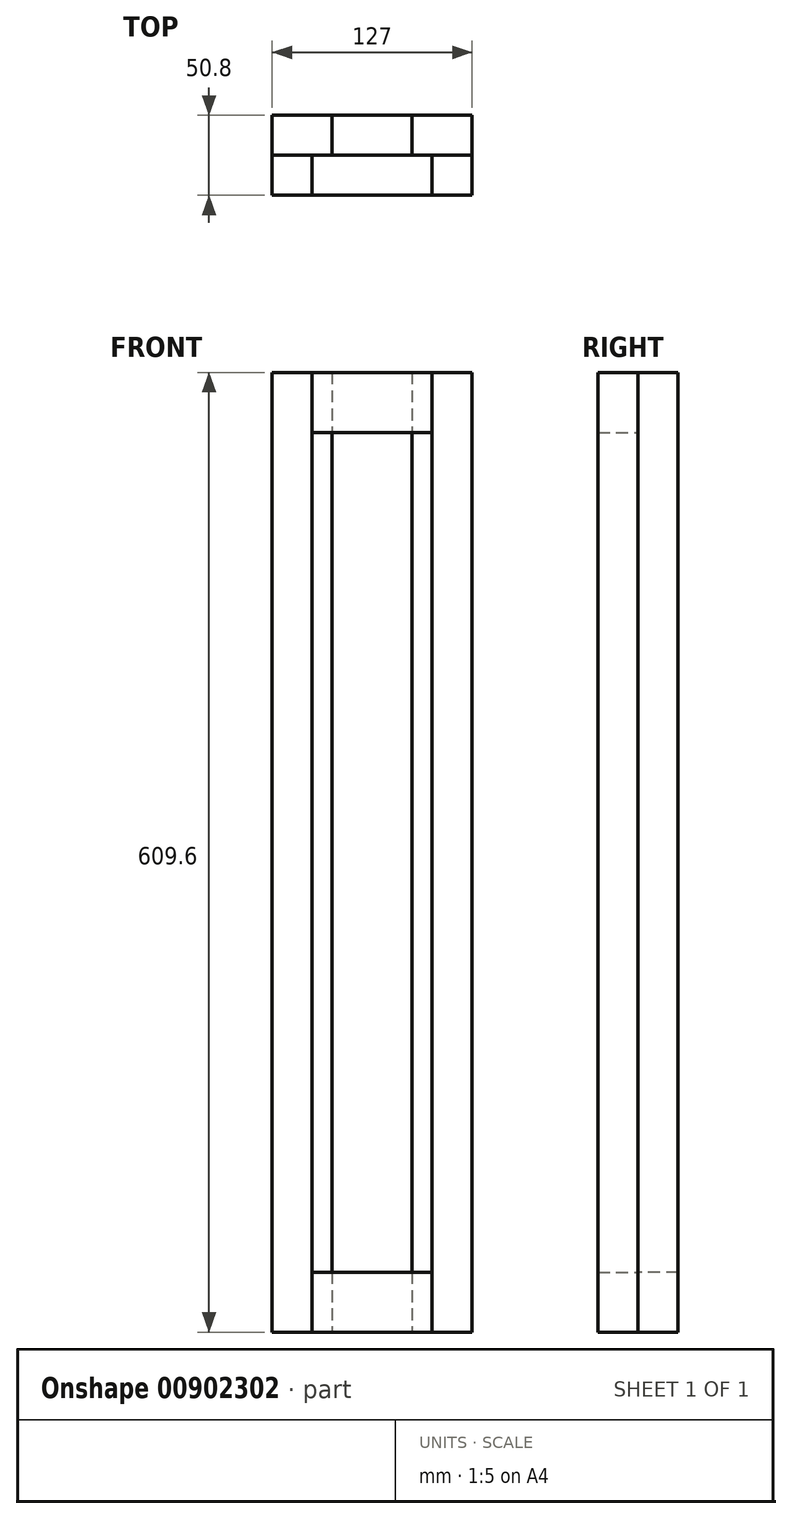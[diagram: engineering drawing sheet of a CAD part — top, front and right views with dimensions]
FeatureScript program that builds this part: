
annotation { "Feature Type Name" : "Feature", "Feature Type Description" : "" }
export const myFeature = defineFeature(function(context is Context, id is Id, definition is map)
    precondition{}
    {
        {
            var Q0;
            Q0=qCreatedBy(makeId("Front.planeOp"),FACE);
            var sketch = newSketch(context, id + "F0", { "sketchPlane" : qUnion([Q0])});
            skLineSegment(sketch, "E0.bottom", {"start": v(-63.5, 256.82) * mm, "end": v(-25.4, 256.82) * mm});
            skLineSegment(sketch, "E0.top", {"start": v(-63.5, -352.78) * mm, "end": v(-25.4, -352.78) * mm});
            skLineSegment(sketch, "E0.left", {"start": v(-63.5, 256.82) * mm, "end": v(-63.5, -352.78) * mm});
            skLineSegment(sketch, "E0.right", {"start": v(-25.4, 256.82) * mm, "end": v(-25.4, -352.78) * mm});
            skLineSegment(sketch, "E1.bottom", {"start": v(25.4, 256.82) * mm, "end": v(63.5, 256.82) * mm});
            skLineSegment(sketch, "E1.top", {"start": v(25.4, -352.78) * mm, "end": v(63.5, -352.78) * mm});
            skLineSegment(sketch, "E1.left", {"start": v(25.4, 256.82) * mm, "end": v(25.4, -352.78) * mm});
            skLineSegment(sketch, "E1.right", {"start": v(63.5, 256.82) * mm, "end": v(63.5, -352.78) * mm});
            skSolve(sketch);
        }
        {
            var Q0;
            Q0=makeQuery(id+"F0.imprint","IMPRINT",FACE,{"disambiguationData":[TD([[makeQuery(id+"F0.imprint","IMPRINT",EDGE,{"derivedFrom":sQuery(id+"F0.wireOp",EDGE,"E1.bottom")}),-1.0]])]});
            var Q1;
            Q1=makeQuery(id+"F0.imprint","IMPRINT",FACE,{"disambiguationData":[TD([[makeQuery(id+"F0.imprint","IMPRINT",EDGE,{"derivedFrom":sQuery(id+"F0.wireOp",EDGE,"E0.bottom")}),-1.0]])]});
            extrude(context, id + "F1", {"entities" : qUnion([Q0, Q1]), "oppositeDirection" : true, "depth" : 25.4 * mm, "offsetDistance" : 25.4 * mm});
        }
        {
            var Q0;
            Q0=qCreatedBy(makeId("Front.planeOp"),FACE);
            var sketch = newSketch(context, id + "F2", { "sketchPlane" : qUnion([Q0])});
            skLineSegment(sketch, "E2.bottom", {"start": v(-63.5, 256.82) * mm, "end": v(-38.1, 256.82) * mm});
            skLineSegment(sketch, "E2.top", {"start": v(-63.5, -352.78) * mm, "end": v(-38.1, -352.78) * mm});
            skLineSegment(sketch, "E2.left", {"start": v(-63.5, 256.82) * mm, "end": v(-63.5, -352.78) * mm});
            skLineSegment(sketch, "E2.right", {"start": v(-38.1, 256.82) * mm, "end": v(-38.1, -352.78) * mm});
            skLineSegment(sketch, "E3.bottom", {"start": v(38.1, 256.82) * mm, "end": v(63.5, 256.82) * mm});
            skLineSegment(sketch, "E3.top", {"start": v(38.1, -352.78) * mm, "end": v(63.5, -352.78) * mm});
            skLineSegment(sketch, "E3.left", {"start": v(38.1, 256.82) * mm, "end": v(38.1, -352.78) * mm});
            skLineSegment(sketch, "E3.right", {"start": v(63.5, 256.82) * mm, "end": v(63.5, -352.78) * mm});
            skLineSegment(sketch, "E4.bottom", {"start": v(-38.1, 256.82) * mm, "end": v(38.1, 256.82) * mm});
            skLineSegment(sketch, "E4.top", {"start": v(-38.1, 218.72) * mm, "end": v(38.1, 218.72) * mm});
            skLineSegment(sketch, "E4.left", {"start": v(-38.1, 256.82) * mm, "end": v(-38.1, 218.72) * mm});
            skLineSegment(sketch, "E4.right", {"start": v(38.1, 256.82) * mm, "end": v(38.1, 218.72) * mm});
            skLineSegment(sketch, "E5.bottom", {"start": v(-38.1, -314.68) * mm, "end": v(38.1, -314.68) * mm});
            skLineSegment(sketch, "E5.top", {"start": v(-38.1, -352.78) * mm, "end": v(38.1, -352.78) * mm});
            skLineSegment(sketch, "E5.left", {"start": v(-38.1, -314.68) * mm, "end": v(-38.1, -352.78) * mm});
            skLineSegment(sketch, "E5.right", {"start": v(38.1, -314.68) * mm, "end": v(38.1, -352.78) * mm});
            skSolve(sketch);
        }
        {
            var Q0;
            Q0=makeQuery(id+"F2.imprint","IMPRINT",FACE,{"disambiguationData":[TD([[makeQuery(id+"F2.imprint","IMPRINT",EDGE,{"derivedFrom":sQuery(id+"F2.wireOp",EDGE,"E2.bottom")}),-1.0]])]});
            var Q1;
            Q1=makeQuery(id+"F2.imprint","IMPRINT",FACE,{"disambiguationData":[TD([[makeQuery(id+"F2.imprint","IMPRINT",EDGE,{"derivedFrom":sQuery(id+"F2.wireOp",EDGE,"E3.bottom")}),-1.0]])]});
            extrude(context, id + "F3", {"entities" : qUnion([Q0, Q1]), "depth" : 25.4 * mm, "offsetDistance" : 25.4 * mm});
        }
        {
            var Q0;
            Q0=makeQuery(id+"F2.imprint","IMPRINT",FACE,{"disambiguationData":[TD([[makeQuery(id+"F2.imprint","IMPRINT",EDGE,{"derivedFrom":sQuery(id+"F2.wireOp",EDGE,"E4.bottom")}),-1.0]])]});
            var Q1;
            Q1=makeQuery(id+"F2.imprint","IMPRINT",FACE,{"disambiguationData":[TD([[makeQuery(id+"F2.imprint","IMPRINT",EDGE,{"derivedFrom":sQuery(id+"F2.wireOp",EDGE,"E5.bottom")}),-1.0]])]});
            extrude(context, id + "F4", {"entities" : qUnion([Q0, Q1]), "depth" : 25.4 * mm, "offsetDistance" : 25.4 * mm});
        }
        {
            var Q0;
            Q0=makeQuery(id+"F4.opExtrude","CAP_FACE",FACE,{"disambiguationData":[OSD([sQuery(id+"F2.wireOp",EDGE,"E5.bottom"),sQuery(id+"F2.wireOp",EDGE,"E5.top"),sQuery(id+"F2.wireOp",EDGE,"E5.left"),sQuery(id+"F2.wireOp",EDGE,"E5.right")])],"isStart":true});
            var sketch = newSketch(context, id + "F5", { "sketchPlane" : qUnion([Q0])});
            skLineSegment(sketch, "E6.bottom", {"start": v(-25.4, -314.68) * mm, "end": v(25.4, -314.68) * mm});
            skLineSegment(sketch, "E6.top", {"start": v(-25.4, -352.78) * mm, "end": v(25.4, -352.78) * mm});
            skLineSegment(sketch, "E6.left", {"start": v(-25.4, -314.68) * mm, "end": v(-25.4, -352.78) * mm});
            skLineSegment(sketch, "E6.right", {"start": v(25.4, -314.68) * mm, "end": v(25.4, -352.78) * mm});
            skSolve(sketch);
        }
        {
            var Q0;
            Q0 = qSketchRegion(id + "F5", true);
            extrude(context, id + "F6", {"entities" : qUnion([Q0]), "depth" : 25.4 * mm, "offsetDistance" : 25.4 * mm});
        }
    });
